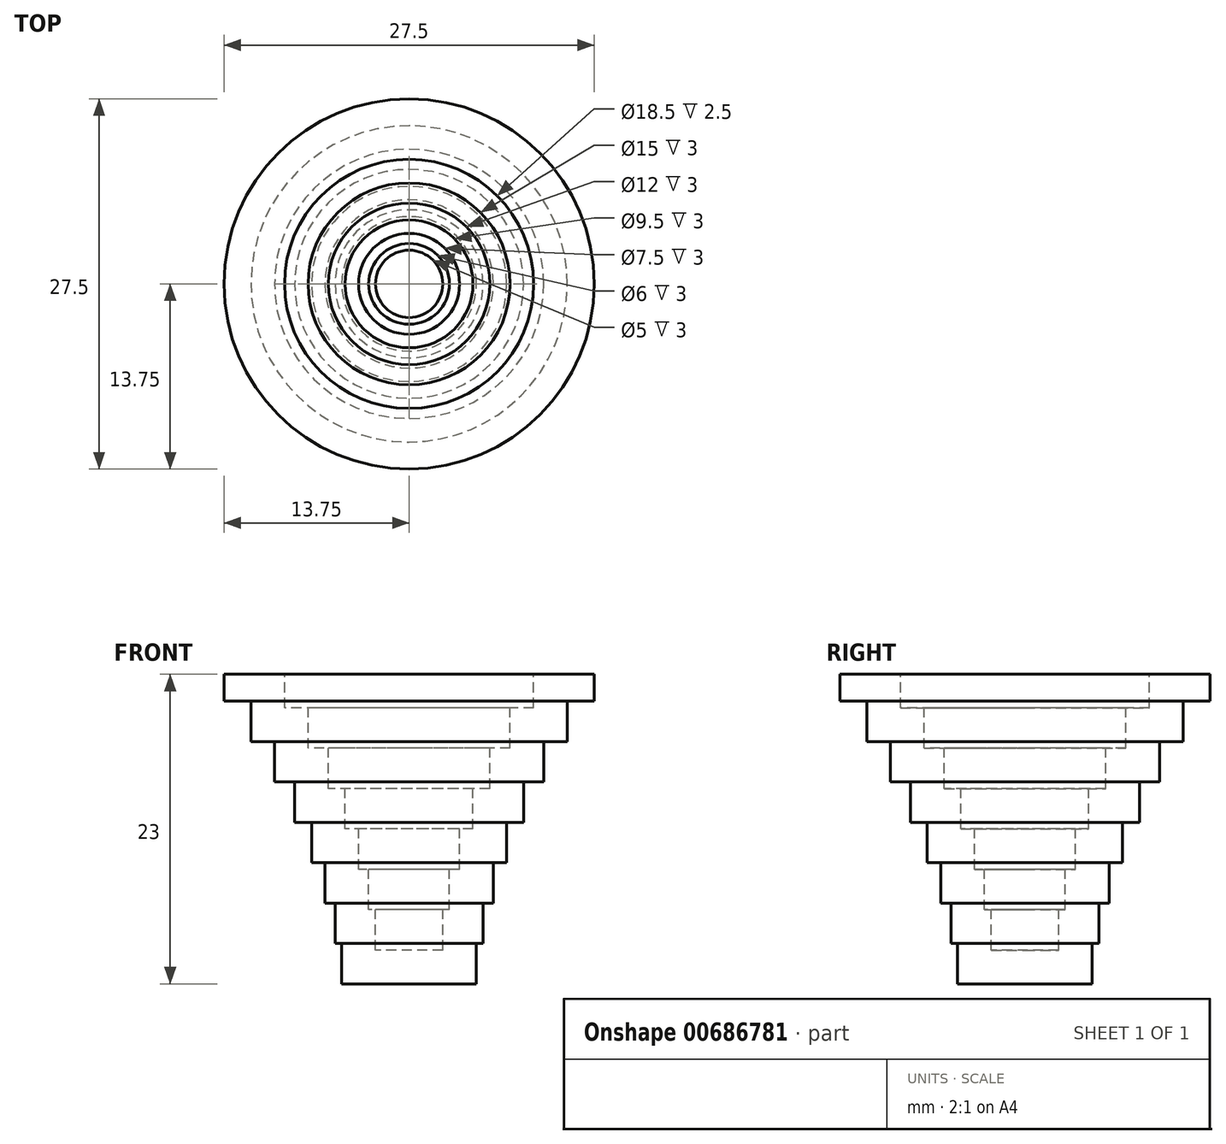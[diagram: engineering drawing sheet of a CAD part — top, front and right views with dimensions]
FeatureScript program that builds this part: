
annotation { "Feature Type Name" : "Feature", "Feature Type Description" : "" }
export const myFeature = defineFeature(function(context is Context, id is Id, definition is map)
    precondition{}
    {
        {
            var Q0;
            Q0=qCreatedBy(makeId("Front.planeOp"),FACE);
            var sketch = newSketch(context, id + "F0", { "sketchPlane" : qUnion([Q0])});
            skLineSegment(sketch, "E0", {"start": v(0, 0) * mm, "end": v(-5, 0) * mm});
            skLineSegment(sketch, "E1", {"start": v(-5, 0) * mm, "end": v(-5, 3) * mm});
            skLineSegment(sketch, "E2", {"start": v(-5, 3) * mm, "end": v(-5.5, 3) * mm});
            skLineSegment(sketch, "E3", {"start": v(-5.5, 3) * mm, "end": v(-5.5, 6) * mm});
            skLineSegment(sketch, "E4", {"start": v(-5.5, 6) * mm, "end": v(-6.25, 6) * mm});
            skLineSegment(sketch, "E5", {"start": v(-6.25, 6) * mm, "end": v(-6.25, 9) * mm});
            skLineSegment(sketch, "E6", {"start": v(-6.25, 9) * mm, "end": v(-7.25, 9) * mm});
            skLineSegment(sketch, "E7", {"start": v(-7.25, 9) * mm, "end": v(-7.25, 12) * mm});
            skLineSegment(sketch, "E8", {"start": v(-7.25, 12) * mm, "end": v(-8.5, 12) * mm});
            skLineSegment(sketch, "E9", {"start": v(-8.5, 12) * mm, "end": v(-8.5, 15) * mm});
            skLineSegment(sketch, "E10", {"start": v(0, 23) * mm, "end": v(0, 0) * mm});
            skLineSegment(sketch, "E11", {"start": v(-8.5, 15) * mm, "end": v(-10, 15) * mm});
            skLineSegment(sketch, "E12", {"start": v(-10, 15) * mm, "end": v(-10, 18) * mm});
            skLineSegment(sketch, "E13", {"start": v(-10, 18) * mm, "end": v(-11.75, 18) * mm});
            skLineSegment(sketch, "E14", {"start": v(-11.75, 18) * mm, "end": v(-11.75, 21) * mm});
            skLineSegment(sketch, "E15", {"start": v(-11.75, 21) * mm, "end": v(-13.75, 21) * mm});
            skLineSegment(sketch, "E16", {"start": v(-13.75, 21) * mm, "end": v(-13.75, 23) * mm});
            skLineSegment(sketch, "E17", {"start": v(-13.75, 23) * mm, "end": v(0, 23) * mm});
            skSolve(sketch);
        }
        {
            var Q0;
            Q0=makeQuery(id+"F0.imprint","IMPRINT",FACE,{"disambiguationData":[TD([[makeQuery(id+"F0.imprint","IMPRINT",EDGE,{"derivedFrom":sQuery(id+"F0.wireOp",EDGE,"E0")}),-1.0]])]});
            var Q1;
            Q1=sQuery(id+"F0.wireOp",EDGE,"E10");
            revolve(context, id + "F1", {"surfaceOperationType" : NewSurfaceOperationType.NEW, "entities" : qUnion([Q0]), "axis" : qUnion([Q1]), "revolveType" : RevolveType.FULL});
        }
        {
            var Q0;
            Q0=makeQuery(id+"F1.opRevolve","SWEPT_FACE",FACE,{"disambiguationData":[OSD([sQuery(id+"F0.wireOp",EDGE,"E17")])]});
            shell(context, id + "F2", {"entities" : qUnion([Q0]), "thickness" : 2.5 * mm});
        }
    });
